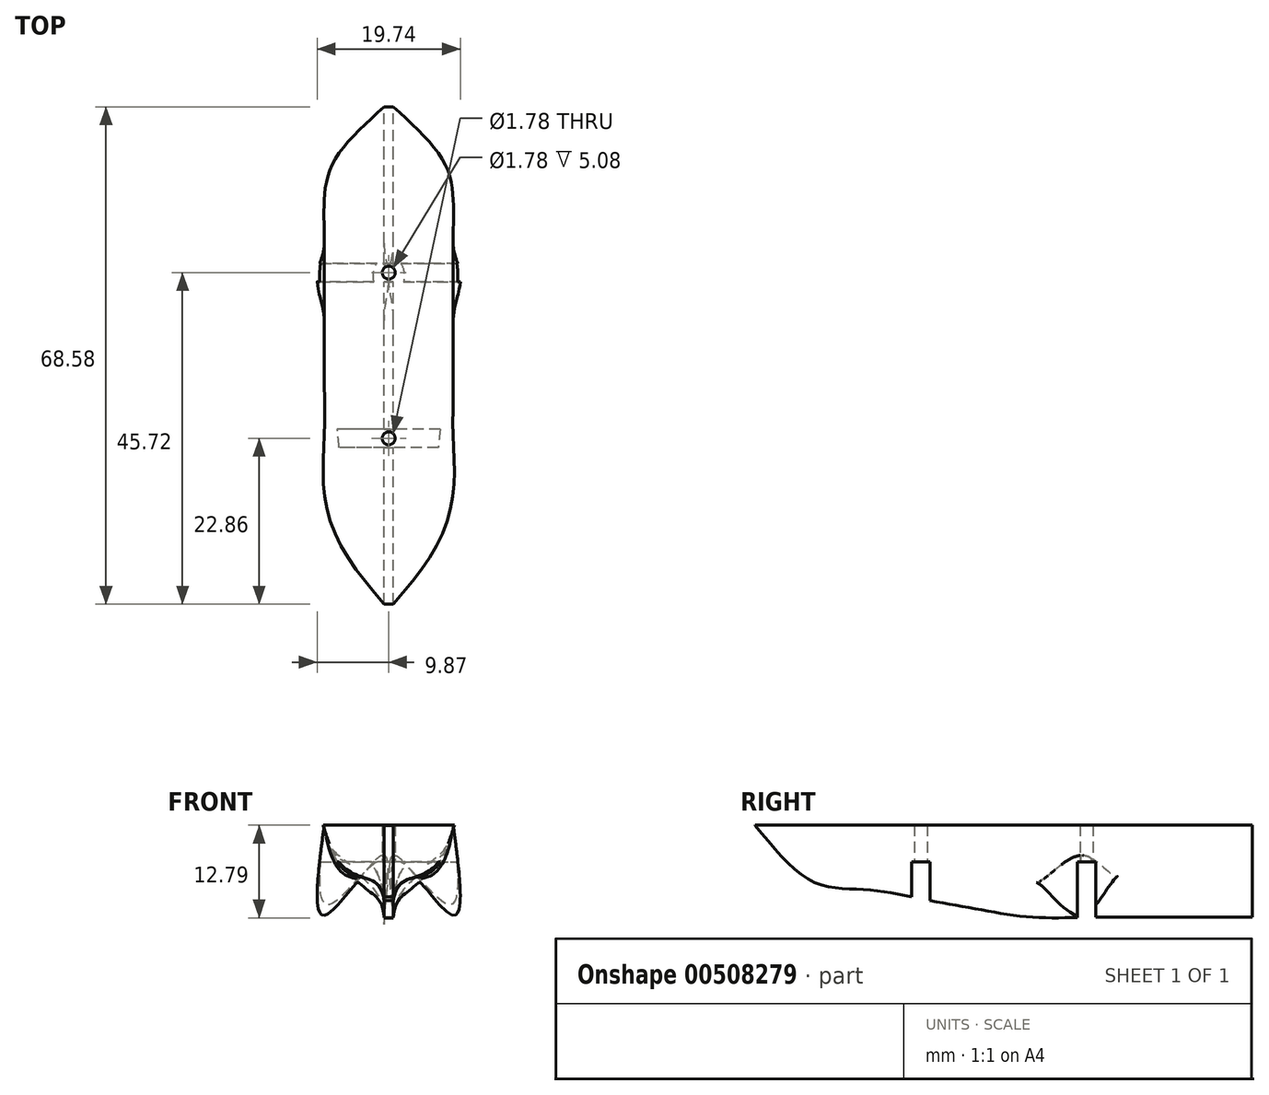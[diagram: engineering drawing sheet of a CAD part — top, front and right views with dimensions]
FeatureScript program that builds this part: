
annotation { "Feature Type Name" : "Feature", "Feature Type Description" : "" }
export const myFeature = defineFeature(function(context is Context, id is Id, definition is map)
    precondition{}
    {
        {
            var Q0;
            Q0=qCreatedBy(makeId("Front.planeOp"),FACE);
            var sketch = newSketch(context, id + "F0", { "sketchPlane" : qUnion([Q0])});
            skLineSegment(sketch, "E0", {"start": v(-8.89, 0) * mm, "end": v(8.89, 0) * mm});
            skLineSegment(sketch, "E1", {"start": v(-0.63, -12.7) * mm, "end": v(0.64, -12.7) * mm});
            skLineSegment(sketch, "E2", {"start": v(0, 6.14) * mm, "end": v(0, -18.6) * mm, "construction": true});
            skFitSpline(sketch, "E3", {"points": [v(-0.63, -12.7) * mm, v(-8.9, 0) * mm], "startDerivative": vector(-1.08, 25.23) * mm, "endDerivative": vector(-0.6, 36.48) * mm});
            skFitSpline(sketch, "E4.MirrorCS", {"points": [v(0.64, -12.7) * mm, v(8.9, 0) * mm], "startDerivative": vector(1.08, 25.23) * mm, "endDerivative": vector(0.6, 36.48) * mm});
            skSolve(sketch);
        }
        {
            var Q0;
            Q0=qCreatedBy(makeId("Front.planeOp"),FACE);
            cPlane(context, id + "F1", {"entities" : qUnion([Q0]), "cplaneType" : CPlaneType.OFFSET, "offset" : 30.48 * mm, "oppositeDirection" : true, "width" : 152.4 * mm, "height" : 152.4 * mm});
        }
        {
            var Q0;
            Q0=qCreatedBy(id+"F1.planeOp",FACE);
            var sketch = newSketch(context, id + "F2", { "sketchPlane" : qUnion([Q0])});
            skLineSegment(sketch, "E5.0", {"start": v(-8.89, 0) * mm, "end": v(8.89, 0) * mm, "construction": true});
            skLineSegment(sketch, "E6.0", {"start": v(-0.63, -12.7) * mm, "end": v(0.64, -12.7) * mm, "construction": true});
            skLineSegment(sketch, "E7.0", {"start": v(0, 6.14) * mm, "end": v(0, -18.6) * mm, "construction": true});
            skLineSegment(sketch, "E8.bottom", {"start": v(-0.63, -12.7) * mm, "end": v(0.62, -12.7) * mm});
            skLineSegment(sketch, "E8.top", {"start": v(-0.63, 0) * mm, "end": v(0.62, 0) * mm});
            skLineSegment(sketch, "E8.left", {"start": v(-0.63, -12.7) * mm, "end": v(-0.63, 0) * mm});
            skLineSegment(sketch, "E8.right", {"start": v(0.62, -12.7) * mm, "end": v(0.62, 0) * mm});
            skCircle(sketch, "E9", {"center": v(0, -3.19) * mm, "radius": 9.9 * mm, "construction": true});
            skSolve(sketch);
        }
        {
            var Q0;
            Q0=qCreatedBy(makeId("Front.planeOp"),FACE);
            cPlane(context, id + "F3", {"entities" : qUnion([Q0]), "cplaneType" : CPlaneType.OFFSET, "offset" : 22.86 * mm, "oppositeDirection" : true, "width" : 152.4 * mm, "height" : 152.4 * mm});
        }
        {
            var Q0;
            Q0=qCreatedBy(id+"F3.planeOp",FACE);
            var sketch = newSketch(context, id + "F4", { "sketchPlane" : qUnion([Q0])});
            skLineSegment(sketch, "E10.0", {"start": v(-8.89, 0) * mm, "end": v(8.89, 0) * mm, "construction": true});
            skLineSegment(sketch, "E11.0", {"start": v(0, 6.14) * mm, "end": v(0, -18.6) * mm, "construction": true});
            skLineSegment(sketch, "E12", {"start": v(7.62, 0) * mm, "end": v(-7.62, 0) * mm});
            skLineSegment(sketch, "E13.0", {"start": v(-0.63, -12.7) * mm, "end": v(0.64, -12.7) * mm, "construction": true});
            skLineSegment(sketch, "E14", {"start": v(0.64, -12.7) * mm, "end": v(-0.64, -12.7) * mm});
            skFitSpline(sketch, "E15", {"points": [v(-0.64, -12.7) * mm, v(-7.62, 0) * mm], "startDerivative": vector(-0.2, 38.1) * mm, "endDerivative": vector(-2.24, 25.31) * mm});
            skFitSpline(sketch, "E16.MirrorCS", {"points": [v(0.64, -12.7) * mm, v(7.62, 0) * mm], "startDerivative": vector(0.2, 38.1) * mm, "endDerivative": vector(2.24, 25.31) * mm});
            skSolve(sketch);
        }
        {
            var Q0;
            Q0=qCreatedBy(makeId("Front.planeOp"),FACE);
            cPlane(context, id + "F5", {"entities" : qUnion([Q0]), "cplaneType" : CPlaneType.OFFSET, "offset" : 17.78 * mm, "oppositeDirection" : true, "width" : 152.4 * mm, "height" : 152.4 * mm});
        }
        {
            var Q0;
            Q0=qCreatedBy(id+"F5.planeOp",FACE);
            var sketch = newSketch(context, id + "F6", { "sketchPlane" : qUnion([Q0])});
            skLineSegment(sketch, "E17.0", {"start": v(0, 6.14) * mm, "end": v(0, -18.6) * mm, "construction": true});
            skLineSegment(sketch, "E18.0", {"start": v(-8.89, 0) * mm, "end": v(8.89, 0) * mm, "construction": true});
            skLineSegment(sketch, "E19.0", {"start": v(-0.63, -12.7) * mm, "end": v(0.64, -12.7) * mm, "construction": true});
            skLineSegment(sketch, "E20", {"start": v(8.89, 0) * mm, "end": v(-8.89, 0) * mm});
            skLineSegment(sketch, "E21", {"start": v(0.64, -12.7) * mm, "end": v(-0.63, -12.7) * mm});
            skFitSpline(sketch, "E22", {"points": [v(8.89, 0) * mm, v(0.64, -12.7) * mm], "startDerivative": vector(-3.53, -27.31) * mm, "endDerivative": vector(-2.5, -33.2) * mm});
            skFitSpline(sketch, "E23.MirrorCS", {"points": [v(-8.89, 0) * mm, v(-0.64, -12.7) * mm], "startDerivative": vector(3.53, -27.31) * mm, "endDerivative": vector(2.5, -33.2) * mm});
            skSolve(sketch);
        }
        {
            var Q0;
            Q0=qCreatedBy(makeId("Front.planeOp"),FACE);
            cPlane(context, id + "F7", {"entities" : qUnion([Q0]), "cplaneType" : CPlaneType.OFFSET, "offset" : 12.7 * mm, "oppositeDirection" : true, "width" : 152.4 * mm, "height" : 152.4 * mm});
        }
        {
            var Q0;
            Q0=qCreatedBy(id+"F7.planeOp",FACE);
            var sketch = newSketch(context, id + "F8", { "sketchPlane" : qUnion([Q0])});
            skLineSegment(sketch, "E24.0", {"start": v(0, 6.14) * mm, "end": v(0, -18.6) * mm, "construction": true});
            skLineSegment(sketch, "E25.0", {"start": v(-8.89, 0) * mm, "end": v(8.89, 0) * mm, "construction": true});
            skLineSegment(sketch, "E26.0", {"start": v(-0.63, -12.7) * mm, "end": v(0.64, -12.7) * mm, "construction": true});
            skLineSegment(sketch, "E27.0.1", {"start": v(-0.63, -12.7) * mm, "end": v(0.64, -12.7) * mm});
            skLineSegment(sketch, "E27.0.3", {"start": v(8.89, 0) * mm, "end": v(-8.89, 0) * mm});
            skFitSpline(sketch, "E28", {"points": [v(8.89, 0) * mm, v(0.64, -12.7) * mm], "startDerivative": vector(-1.03, -28.98) * mm, "endDerivative": vector(-1.31, -26.3) * mm});
            skFitSpline(sketch, "E29.MirrorCS", {"points": [v(-8.89, 0) * mm, v(-0.64, -12.7) * mm], "startDerivative": vector(1.03, -28.98) * mm, "endDerivative": vector(1.31, -26.3) * mm});
            skSolve(sketch);
        }
        {
            var Q0;
            Q0=qCreatedBy(makeId("Front.planeOp"),FACE);
            cPlane(context, id + "F9", {"entities" : qUnion([Q0]), "cplaneType" : CPlaneType.OFFSET, "offset" : 7.62 * mm, "oppositeDirection" : true, "width" : 152.4 * mm, "height" : 152.4 * mm});
        }
        {
            var Q0;
            Q0=qCreatedBy(id+"F9.planeOp",FACE);
            var sketch = newSketch(context, id + "F10", { "sketchPlane" : qUnion([Q0])});
            skLineSegment(sketch, "E30.0", {"start": v(-8.89, 0) * mm, "end": v(8.89, 0) * mm, "construction": true});
            skLineSegment(sketch, "E31.0", {"start": v(0, 6.14) * mm, "end": v(0, -18.6) * mm, "construction": true});
            skLineSegment(sketch, "E32.0", {"start": v(-0.63, -12.7) * mm, "end": v(0.64, -12.7) * mm, "construction": true});
            skLineSegment(sketch, "E33", {"start": v(-8.89, 0) * mm, "end": v(8.89, 0) * mm});
            skLineSegment(sketch, "E34", {"start": v(0.64, -12.7) * mm, "end": v(-0.63, -12.7) * mm});
            skFitSpline(sketch, "E35.0.0", {"points": [v(-8.9, 0) * mm, v(-8.7, -12.16) * mm, v(-1, -4.29) * mm, v(-0.63, -12.7) * mm]});
            skLineSegment(sketch, "E35.0.1", {"start": v(-0.63, -12.7) * mm, "end": v(0.64, -12.7) * mm});
            skFitSpline(sketch, "E35.0.2", {"points": [v(0.64, -12.7) * mm, v(1, -4.29) * mm, v(8.7, -12.16) * mm, v(8.9, 0) * mm]});
            skLineSegment(sketch, "E35.0.3", {"start": v(8.89, 0) * mm, "end": v(-8.89, 0) * mm});
            skSolve(sketch);
        }
        {
            var Q0;
            Q0=qCreatedBy(makeId("Front.planeOp"),FACE);
            cPlane(context, id + "F11", {"entities" : qUnion([Q0]), "cplaneType" : CPlaneType.OFFSET, "offset" : 7.62 * mm, "width" : 152.4 * mm, "height" : 152.4 * mm});
        }
        {
            var Q0;
            Q0=qCreatedBy(id+"F11.planeOp",FACE);
            var sketch = newSketch(context, id + "F12", { "sketchPlane" : qUnion([Q0])});
            skLineSegment(sketch, "E36.0", {"start": v(0, 6.14) * mm, "end": v(0, -18.6) * mm, "construction": true});
            skLineSegment(sketch, "E36.1", {"start": v(-8.89, 0) * mm, "end": v(8.89, 0) * mm, "construction": true});
            skLineSegment(sketch, "E36.2", {"start": v(-0.63, -12.7) * mm, "end": v(0.64, -12.7) * mm, "construction": true});
            skLineSegment(sketch, "E37", {"start": v(-8.89, 0) * mm, "end": v(8.89, 0) * mm});
            skLineSegment(sketch, "E38", {"start": v(0.64, -12.7) * mm, "end": v(-0.63, -12.7) * mm});
            skLineSegment(sketch, "E39", {"start": v(-0.64, -11.56) * mm, "end": v(0.64, -11.56) * mm});
            skFitSpline(sketch, "E40", {"points": [v(0.64, -11.56) * mm, v(8.89, 0) * mm], "startDerivative": vector(2.4, 22.73) * mm, "endDerivative": vector(4.67, 35.63) * mm});
            skFitSpline(sketch, "E41.MirrorCS", {"points": [v(-0.64, -11.56) * mm, v(-8.89, 0) * mm], "startDerivative": vector(-2.4, 22.73) * mm, "endDerivative": vector(-4.67, 35.63) * mm});
            skSolve(sketch);
        }
        {
            var Q0;
            Q0=qCreatedBy(makeId("Front.planeOp"),FACE);
            cPlane(context, id + "F13", {"entities" : qUnion([Q0]), "cplaneType" : CPlaneType.OFFSET, "offset" : 15.24 * mm, "width" : 152.4 * mm, "height" : 152.4 * mm});
        }
        {
            var Q0;
            Q0=qCreatedBy(id+"F13.planeOp",FACE);
            var sketch = newSketch(context, id + "F14", { "sketchPlane" : qUnion([Q0])});
            skLineSegment(sketch, "E42.0", {"start": v(-8.89, 0) * mm, "end": v(8.89, 0) * mm, "construction": true});
            skLineSegment(sketch, "E42.1", {"start": v(0, 6.14) * mm, "end": v(0, -18.6) * mm, "construction": true});
            skLineSegment(sketch, "E42.2", {"start": v(-0.63, -12.7) * mm, "end": v(0.64, -12.7) * mm, "construction": true});
            skLineSegment(sketch, "E43", {"start": v(-8.89, 0) * mm, "end": v(8.89, 0) * mm});
            skLineSegment(sketch, "E44", {"start": v(-0.64, -10.16) * mm, "end": v(0.64, -10.16) * mm});
            skFitSpline(sketch, "E45", {"points": [v(-8.89, 0) * mm, v(-0.64, -10.16) * mm], "startDerivative": vector(6.63, -31.48) * mm, "endDerivative": vector(3.55, -16.3) * mm});
            skFitSpline(sketch, "E46.MirrorCS", {"points": [v(8.89, 0) * mm, v(0.64, -10.16) * mm], "startDerivative": vector(-6.63, -31.48) * mm, "endDerivative": vector(-3.55, -16.3) * mm});
            skSolve(sketch);
        }
        {
            var Q0;
            Q0=qCreatedBy(makeId("Front.planeOp"),FACE);
            cPlane(context, id + "F15", {"entities" : qUnion([Q0]), "cplaneType" : CPlaneType.OFFSET, "offset" : 22.86 * mm, "width" : 152.4 * mm, "height" : 152.4 * mm});
        }
        {
            var Q0;
            Q0=qCreatedBy(id+"F15.planeOp",FACE);
            var sketch = newSketch(context, id + "F16", { "sketchPlane" : qUnion([Q0])});
            skLineSegment(sketch, "E47.0", {"start": v(0, 6.14) * mm, "end": v(0, -18.6) * mm, "construction": true});
            skLineSegment(sketch, "E47.1", {"start": v(-8.89, 0) * mm, "end": v(8.89, 0) * mm, "construction": true});
            skLineSegment(sketch, "E47.2", {"start": v(-0.63, -12.7) * mm, "end": v(0.64, -12.7) * mm, "construction": true});
            skLineSegment(sketch, "E48", {"start": v(-8.89, 0) * mm, "end": v(8.89, 0) * mm});
            skLineSegment(sketch, "E49", {"start": v(-0.64, -8.9) * mm, "end": v(0.64, -8.9) * mm});
            skFitSpline(sketch, "E50", {"points": [v(-8.89, 0) * mm, v(-0.64, -8.9) * mm], "startDerivative": vector(7.84, -27.47) * mm, "endDerivative": vector(4.38, -10.38) * mm});
            skFitSpline(sketch, "E51.MirrorCS", {"points": [v(8.89, 0) * mm, v(0.64, -8.9) * mm], "startDerivative": vector(-7.84, -27.47) * mm, "endDerivative": vector(-4.38, -10.38) * mm});
            skSolve(sketch);
        }
        {
            var Q0;
            Q0=qCreatedBy(makeId("Front.planeOp"),FACE);
            cPlane(context, id + "F17", {"entities" : qUnion([Q0]), "cplaneType" : CPlaneType.OFFSET, "offset" : 30.48 * mm, "width" : 152.4 * mm, "height" : 152.4 * mm});
        }
        {
            var Q0;
            Q0=qCreatedBy(id+"F17.planeOp",FACE);
            var sketch = newSketch(context, id + "F18", { "sketchPlane" : qUnion([Q0])});
            skLineSegment(sketch, "E52.0", {"start": v(0, 6.14) * mm, "end": v(0, -18.6) * mm, "construction": true});
            skLineSegment(sketch, "E52.1", {"start": v(-8.89, 0) * mm, "end": v(8.89, 0) * mm, "construction": true});
            skLineSegment(sketch, "E52.2", {"start": v(-0.63, -12.7) * mm, "end": v(0.64, -12.7) * mm, "construction": true});
            skLineSegment(sketch, "E53", {"start": v(-6.35, 0) * mm, "end": v(6.35, 0) * mm});
            skLineSegment(sketch, "E54", {"start": v(-0.64, -7.62) * mm, "end": v(0.64, -7.62) * mm});
            skFitSpline(sketch, "E55", {"points": [v(-6.35, 0) * mm, v(-0.64, -7.62) * mm], "startDerivative": vector(2.78, -18.97) * mm, "endDerivative": vector(2.94, -8.6) * mm});
            skFitSpline(sketch, "E56.MirrorCS", {"points": [v(6.35, 0) * mm, v(0.64, -7.62) * mm], "startDerivative": vector(-2.78, -18.97) * mm, "endDerivative": vector(-2.94, -8.6) * mm});
            skSolve(sketch);
        }
        {
            var Q0;
            Q0=qCreatedBy(makeId("Front.planeOp"),FACE);
            cPlane(context, id + "F19", {"entities" : qUnion([Q0]), "cplaneType" : CPlaneType.OFFSET, "offset" : 38.1 * mm, "width" : 152.4 * mm, "height" : 152.4 * mm});
        }
        {
            var Q0;
            Q0=qCreatedBy(id+"F19.planeOp",FACE);
            var sketch = newSketch(context, id + "F20", { "sketchPlane" : qUnion([Q0])});
            skLineSegment(sketch, "E57.0", {"start": v(0, 6.14) * mm, "end": v(0, -18.6) * mm, "construction": true});
            skLineSegment(sketch, "E57.1", {"start": v(-8.89, 0) * mm, "end": v(8.89, 0) * mm, "construction": true});
            skLineSegment(sketch, "E57.2", {"start": v(-0.63, -12.7) * mm, "end": v(0.64, -12.7) * mm, "construction": true});
            skLineSegment(sketch, "E58.bottom", {"start": v(-0.64, 0) * mm, "end": v(0.64, 0) * mm});
            skLineSegment(sketch, "E58.top", {"start": v(-0.64, -0.03) * mm, "end": v(0.64, -0.03) * mm});
            skLineSegment(sketch, "E58.left", {"start": v(-0.64, 0) * mm, "end": v(-0.64, -0.03) * mm});
            skLineSegment(sketch, "E58.right", {"start": v(0.64, 0) * mm, "end": v(0.64, -0.03) * mm});
            skSolve(sketch);
        }
        {
            var Q0;
            Q0=makeQuery(id+"F20.imprint","IMPRINT",FACE,{"disambiguationData":[TD([[makeQuery(id+"F20.imprint","IMPRINT",EDGE,{"derivedFrom":sQuery(id+"F20.wireOp",EDGE,"E58.bottom")}),-1.0]])]});
            var Q1;
            Q1=makeQuery(id+"F18.imprint","IMPRINT",FACE,{"disambiguationData":[TD([[makeQuery(id+"F18.imprint","IMPRINT",EDGE,{"derivedFrom":sQuery(id+"F18.wireOp",EDGE,"E53")}),-1.0]])]});
            var Q2;
            Q2=makeQuery(id+"F16.imprint","IMPRINT",FACE,{"disambiguationData":[TD([[makeQuery(id+"F16.imprint","IMPRINT",EDGE,{"derivedFrom":sQuery(id+"F16.wireOp",EDGE,"E48")}),-1.0]])]});
            var Q3;
            Q3=makeQuery(id+"F14.imprint","IMPRINT",FACE,{"disambiguationData":[TD([[makeQuery(id+"F14.imprint","IMPRINT",EDGE,{"derivedFrom":sQuery(id+"F14.wireOp",EDGE,"E43")}),-1.0]])]});
            var Q4;
            Q4=makeQuery(id+"F12.imprint","IMPRINT",FACE,{"disambiguationData":[TD([[makeQuery(id+"F12.imprint","IMPRINT",EDGE,{"derivedFrom":sQuery(id+"F12.wireOp",EDGE,"E37")}),-1.0]])]});
            var Q5;
            Q5=makeQuery(id+"F0.imprint","IMPRINT",FACE,{"disambiguationData":[TD([[makeQuery(id+"F0.imprint","IMPRINT",EDGE,{"derivedFrom":sQuery(id+"F0.wireOp",EDGE,"E0")}),-1.0]])]});
            var Q6;
            Q6=makeQuery(id+"F10.imprint","IMPRINT",FACE,{"disambiguationData":[TD([[makeQuery(id+"F10.imprint","IMPRINT",EDGE,{"derivedFrom":sQuery(id+"F10.wireOp",EDGE,"E35.0.0")}),1.0]])]});
            var Q7;
            Q7=makeQuery(id+"F8.imprint","IMPRINT",FACE,{"disambiguationData":[TD([[makeQuery(id+"F8.imprint","IMPRINT",EDGE,{"derivedFrom":sQuery(id+"F8.wireOp",EDGE,"E27.0.1")}),1.0]])]});
            var Q8;
            Q8=makeQuery(id+"F6.imprint","IMPRINT",FACE,{"disambiguationData":[TD([[makeQuery(id+"F6.imprint","IMPRINT",EDGE,{"derivedFrom":sQuery(id+"F6.wireOp",EDGE,"E20")}),1.0]])]});
            var Q9;
            Q9=makeQuery(id+"F4.imprint","IMPRINT",FACE,{"disambiguationData":[TD([[makeQuery(id+"F4.imprint","IMPRINT",EDGE,{"derivedFrom":sQuery(id+"F4.wireOp",EDGE,"E12")}),1.0]])]});
            var Q10;
            Q10=makeQuery(id+"F2.imprint","IMPRINT",FACE,{"disambiguationData":[TD([[makeQuery(id+"F2.imprint","IMPRINT",EDGE,{"derivedFrom":sQuery(id+"F2.wireOp",EDGE,"E8.bottom")}),1.0]])]});
            loft(context, id + "F21", {"sheetProfilesArray" : [{ "sheetProfileEntities" : qUnion([Q0]) }, { "sheetProfileEntities" : qUnion([Q1]) }, { "sheetProfileEntities" : qUnion([Q2]) }, { "sheetProfileEntities" : qUnion([Q3]) }, { "sheetProfileEntities" : qUnion([Q4]) }, { "sheetProfileEntities" : qUnion([Q5]) }, { "sheetProfileEntities" : qUnion([Q6]) }, { "sheetProfileEntities" : qUnion([Q7]) }, { "sheetProfileEntities" : qUnion([Q8]) }, { "sheetProfileEntities" : qUnion([Q9]) }, { "sheetProfileEntities" : qUnion([Q10]) }]});
        }
        {
            var Q0;
            Q0=qCreatedBy(id+"F9.planeOp",FACE);
            var sketch = newSketch(context, id + "F22", { "sketchPlane" : qUnion([Q0])});
            skLineSegment(sketch, "E59.bottom", {"start": v(-11.55, -5.08) * mm, "end": v(13.55, -5.08) * mm});
            skLineSegment(sketch, "E59.top", {"start": v(-11.55, -15.2) * mm, "end": v(13.55, -15.2) * mm});
            skLineSegment(sketch, "E59.left", {"start": v(-11.55, -5.08) * mm, "end": v(-11.55, -15.2) * mm});
            skLineSegment(sketch, "E59.right", {"start": v(13.55, -5.08) * mm, "end": v(13.55, -15.2) * mm});
            skLineSegment(sketch, "E60.0", {"start": v(-8.89, 0) * mm, "end": v(8.89, 0) * mm, "construction": true});
            skSolve(sketch);
        }
        {
            var Q0;
            Q0=qCreatedBy(id+"F13.planeOp",FACE);
            var sketch = newSketch(context, id + "F23", { "sketchPlane" : qUnion([Q0])});
            skLineSegment(sketch, "E61.0.0", {"start": v(-11.55, -5.08) * mm, "end": v(-11.55, -15.2) * mm});
            skLineSegment(sketch, "E61.0.1", {"start": v(-11.55, -15.2) * mm, "end": v(13.55, -15.2) * mm});
            skLineSegment(sketch, "E61.0.2", {"start": v(13.55, -15.2) * mm, "end": v(13.55, -5.08) * mm});
            skLineSegment(sketch, "E61.0.3", {"start": v(13.55, -5.08) * mm, "end": v(-11.55, -5.08) * mm});
            skSolve(sketch);
        }
        {
            var Q0;
            Q0=makeQuery(id+"F22.imprint","IMPRINT",FACE,{"disambiguationData":[TD([[makeQuery(id+"F22.imprint","IMPRINT",EDGE,{"derivedFrom":sQuery(id+"F22.wireOp",EDGE,"E59.bottom")}),-1.0]])]});
            var Q1;
            Q1=makeQuery(id+"F23.imprint","IMPRINT",FACE,{"disambiguationData":[TD([[makeQuery(id+"F23.imprint","IMPRINT",EDGE,{"derivedFrom":sQuery(id+"F23.wireOp",EDGE,"E61.0.0")}),1.0]])]});
            extrude(context, id + "F24", {"entities" : qUnion([Q0, Q1]), "operationType" : NewBodyOperationType.REMOVE, "endBound" : BoundingType.SYMMETRIC, "oppositeDirection" : true, "depth" : 2.54 * mm});
        }
        {
            var Q0;
            Q0=makeQuery(id+"F24.boolean.opBoolean","COPY",FACE,{"derivedFrom":makeQuery(id+"F24.opExtrude","SWEPT_FACE",FACE,{"disambiguationData":[OSD([sQuery(id+"F23.wireOp",EDGE,"E61.0.3")])]})});
            var sketch = newSketch(context, id + "F25", { "sketchPlane" : qUnion([Q0])});
            skLineSegment(sketch, "E62", {"start": v(0, 16.51) * mm, "end": v(0, 13.97) * mm, "construction": true});
            skLineSegment(sketch, "E63", {"start": v(0, -8.9) * mm, "end": v(0, -6.35) * mm, "construction": true});
            skCircle(sketch, "E64", {"center": v(0, -7.62) * mm, "radius": 0.89 * mm});
            skCircle(sketch, "E65", {"center": v(0, 15.24) * mm, "radius": 0.89 * mm});
            skSolve(sketch);
        }
        {
            var Q0;
            Q0 = qSketchRegion(id + "F25", true);
            extrude(context, id + "F26", {"entities" : qUnion([Q0]), "operationType" : NewBodyOperationType.REMOVE, "endBound" : BoundingType.THROUGH_ALL, "oppositeDirection" : true, "depth" : 25.4 * mm});
        }
    });
